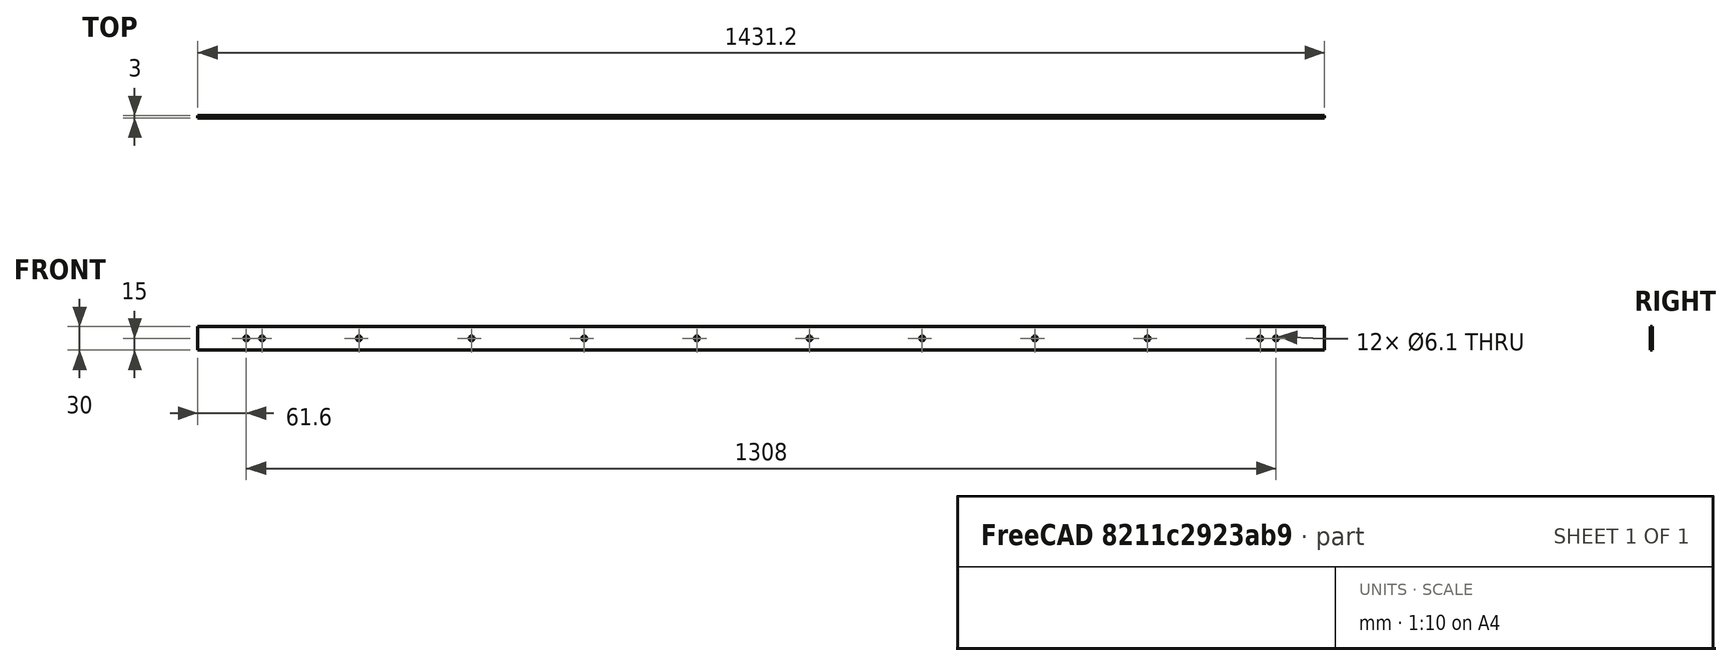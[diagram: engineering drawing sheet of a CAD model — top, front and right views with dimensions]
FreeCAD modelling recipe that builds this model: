
FCSTD DOCUMENT  (FreeCAD 0.15R4671 (Git))
Label: gabarit critique
License: All rights reserved
LicenseURL: http://en.wikipedia.org/wiki/All_rights_reserved
objects: Sketcher::SketchObject×1, PartDesign::Pad×1
note: 3 computed .brp shape members not serialized (recipe doc carries the construction recipe); baked Part::Feature solids carry a one-line shape summary decoded from their .brp

FEATURE [Sketcher::SketchObject] Sketch
  Placement = pos=(0,0,0) rot=(1,0,0;1.5708rad)
  sketch-geometry (16):
    g0: Circle CenterX=-10.05 CenterY=0 CenterZ=0 NormalX=0 NormalY=0 NormalZ=1 Radius=3.05
    g1: Circle CenterX=10.05 CenterY=0 CenterZ=0 NormalX=0 NormalY=0 NormalZ=1 Radius=3.05
    g2: LineSegment StartX=-71.65 StartY=15 StartZ=0 EndX=1359.55 EndY=15 EndZ=0
    g3: LineSegment StartX=1359.55 StartY=15 StartZ=0 EndX=1359.55 EndY=-15 EndZ=0
    g4: LineSegment StartX=1359.55 StartY=-15 StartZ=0 EndX=-71.65 EndY=-15 EndZ=0
    g5: LineSegment StartX=-71.65 StartY=-15 StartZ=0 EndX=-71.65 EndY=15 EndZ=0
    g6: Circle CenterX=133.05 CenterY=0 CenterZ=0 NormalX=0 NormalY=0 NormalZ=1 Radius=3.05
    g7: Circle CenterX=276.15 CenterY=0 CenterZ=0 NormalX=0 NormalY=0 NormalZ=1 Radius=3.05
    g8: Circle CenterX=419.25 CenterY=0 CenterZ=0 NormalX=0 NormalY=0 NormalZ=1 Radius=3.05
    g9: Circle CenterX=562.35 CenterY=0 CenterZ=0 NormalX=0 NormalY=0 NormalZ=1 Radius=3.05
    g10: Circle CenterX=705.45 CenterY=0 CenterZ=0 NormalX=0 NormalY=0 NormalZ=1 Radius=3.05
    g11: Circle CenterX=848.55 CenterY=0 CenterZ=0 NormalX=0 NormalY=0 NormalZ=1 Radius=3.05
    g12: Circle CenterX=991.65 CenterY=0 CenterZ=0 NormalX=0 NormalY=0 NormalZ=1 Radius=3.05
    g13: Circle CenterX=1134.75 CenterY=0 CenterZ=0 NormalX=0 NormalY=0 NormalZ=1 Radius=3.05
    g14: Circle CenterX=1277.85 CenterY=0 CenterZ=0 NormalX=0 NormalY=0 NormalZ=1 Radius=3.05
    g15: Circle CenterX=1297.95 CenterY=0 CenterZ=0 NormalX=0 NormalY=0 NormalZ=1 Radius=3.05
  constraints (49):
    c: PointOnObject(g0,g-1)
    c: PointOnObject(g1,g-1)
    c: Symmetric(g0,g1,g-2)
    c: DistanceX(g0,g1) = 20.1
    c: Coincident(g2,g3)
    c: Coincident(g3,g4)
    c: Coincident(g4,g5)
    c: Coincident(g5,g2)
    c: Horizontal(g2)
    c: Horizontal(g4)
    c: Vertical(g3)
    c: Vertical(g5)
    c: DistanceY(g5) = 30
    c: Symmetric(g2,g4,g-1)
    c: PointOnObject(g6,g-1)
    c: Radius(g0) = 3.05
    c: Equal(g0,g1)
    c: Equal(g0,g6)
    c: DistanceX(g0,g6) = 143.1
    c: DistanceX(g2,g0) = 61.6
    c: PointOnObject(g7,g-1)
    c: PointOnObject(g8,g-1)
    c: PointOnObject(g9,g-1)
    c: PointOnObject(g10,g-1)
    c: PointOnObject(g11,g-1)
    c: PointOnObject(g12,g-1)
    c: PointOnObject(g13,g-1)
    c: PointOnObject(g14,g-1)
    c: PointOnObject(g15,g-1)
    c: Equal(g0,g7)
    c: Equal(g7,g8)
    c: Equal(g8,g9)
    c: Equal(g9,g10)
    c: Equal(g10,g11)
    c: Equal(g11,g13)
    c: Equal(g13,g12)
    c: Equal(g12,g14)
    c: Equal(g14,g15)
    c: DistanceX(g15,g2) = 61.6
    c: DistanceX(g14,g15) = 20.1
    c: DistanceX(g14,g13) = -143.1
    c: DistanceX(g12,g13) = 143.1
    c: DistanceX(g11,g12) = 143.1
    c: DistanceX(g10,g11) = 143.1
    c: DistanceX(g9,g10) = 143.1
    c: DistanceX(g8,g9) = 143.1
    c: DistanceX(g7,g8) = 143.1
    c: DistanceX(g6,g7) = 143.1
    c: DistanceX(g4) = -1431.2
FEATURE [PartDesign::Pad] Pad
  Length = 3
  Length2 = 100
  Placement = pos=(0,0,0) rot=(1,0,0;1.5708rad)
  Sketch = -> Sketch
  Type = 0
